# Revit family: AP
name_source: partatom
category: 機械設備
units: mm (PartAtom-declared; Revit-internal decimal feet)

## family parameters
OmniClass タイトル = Climate Control (HVAC)
OmniClass 番号 = 23.75.00.00
パーツ タイプ = 標準
ロード時にボイドで切り取り = いいえ
丸型コネクタ寸法 = 直径を使用
作業面ベース = いいえ
共有 = いいえ
常に垂直 = はい
部屋計算ポイント = いいえ

## types (4) — shared parameters
URL = http://www.3you.co.jp
製造元 = 株式会社サンユー
zero-valued in all types: 既定の高さ

## per-type parameters (varying)
| type | APp | D | H | L | a | b | c | d | e | t |
| 50x50x75x4.5 | APp : 50x50x75x4.5 | 50  [stored 0.164042 ft] | 50  [stored 0.164042 ft] | 75 | 10  [stored 0.0328084 ft] | 12.75 | 10  [stored 0.0328084 ft] | 12.75 | 25  [stored 0.082021 ft] | 4.5  [stored 0.0147638 ft] |
| 50x50x50x4.5 | APp : 50x50x50x4.5 | 50  [stored 0.164042 ft] | 50  [stored 0.164042 ft] | 50  [stored 0.164042 ft] | 10  [stored 0.0328084 ft] | 12.75 | 10  [stored 0.0328084 ft] | 12.75 | 15  [stored 0.0492126 ft] | 4.5  [stored 0.0147638 ft] |
| 35x30x50x3.2 | APp : 35x30x50x3.2 | 35  [stored 0.114829 ft] | 30  [stored 0.0984252 ft] | 50  [stored 0.164042 ft] | 8.75  [stored 0.0287073 ft] | 8.75  [stored 0.0287073 ft] | 7.5  [stored 0.0246063 ft] | 7.5  [stored 0.0246063 ft] | 16.25  [stored 0.0533136 ft] | 3.2  [stored 0.0104987 ft] |
| 35x30x35x3.2 | APp : 35x30x35x3.2 | 35  [stored 0.114829 ft] | 30  [stored 0.0984252 ft] | 35  [stored 0.114829 ft] | 8.75  [stored 0.0287073 ft] | 8.75  [stored 0.0287073 ft] | 7.5  [stored 0.0246063 ft] | 7.5  [stored 0.0246063 ft] | 11  [stored 0.0360892 ft] | 3.2  [stored 0.0104987 ft] |

note: [stored X ft] marks values corroborated as IEEE doubles in the binary element streams (Revit-internal decimal feet)
